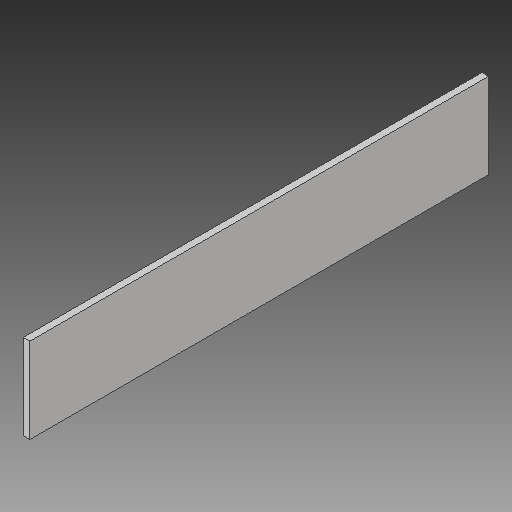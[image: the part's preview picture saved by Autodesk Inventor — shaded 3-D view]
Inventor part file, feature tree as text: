
AUTODESK INVENTOR PART (.ipt)
format: ipt  version: 2017 (Build 210142000, 142)  size: 92,160 bytes
history: native  units: in
note: dims shown in document units (in); Inventor stores cm internally (conversion verified against a paired STEP export)
features: extrude x1, sketch x1
ambient origin geometry x8: Origin, YZ Plane, XZ Plane, XY Plane, X Axis, Y Axis, Z Axis, Center Point
bodies: Solid1 (feature_tree)
feature tree (2):
  extrude  "Extrusion1"  Depth=17.5in
  sketch  "Sketch1"  dims[d2=3.25in d3=17.5in d4=2.0in d5=1.0in d6=2.0in d7=1.0in d8=0.25in d9=0.0in]
